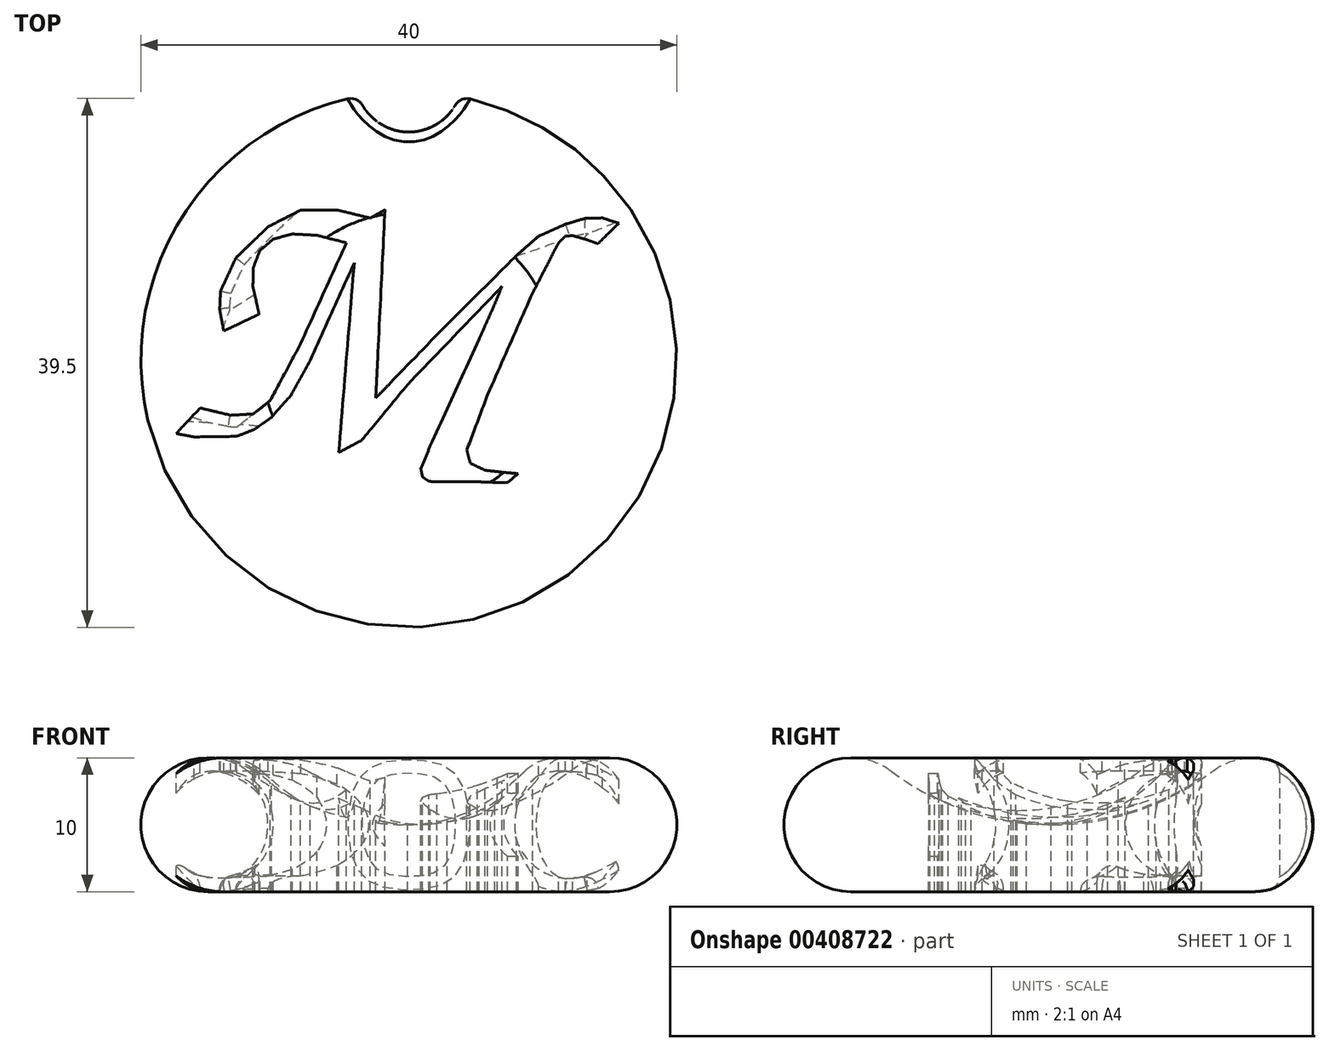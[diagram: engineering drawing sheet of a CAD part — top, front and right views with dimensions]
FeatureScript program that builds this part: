
annotation { "Feature Type Name" : "Feature", "Feature Type Description" : "" }
export const myFeature = defineFeature(function(context is Context, id is Id, definition is map)
    precondition{}
    {
        {
            var Q0;
            Q0=qCreatedBy(makeId("Front.planeOp"),FACE);
            var sketch = newSketch(context, id + "F0", { "sketchPlane" : qUnion([Q0])});
            skArc(sketch, "E0", {"start": v(-12, 9) * mm, "mid": v(-19.74, 6.58) * mm, "end": v(-15, 0) * mm});
            skArc(sketch, "E1", {"start": v(-12, 9) * mm, "mid": v(-6.32, 6.03) * mm, "end": v(0, 5) * mm});
            skLineSegment(sketch, "E2", {"start": v(-15, 0) * mm, "end": v(0, 0) * mm});
            skLineSegment(sketch, "E3", {"start": v(0, 0) * mm, "end": v(0, 5) * mm});
            skSolve(sketch);
        }
        {
            var Q0;
            Q0=makeQuery(id+"F0.imprint","IMPRINT",FACE,{"disambiguationData":[TD([[makeQuery(id+"F0.imprint","IMPRINT",EDGE,{"derivedFrom":sQuery(id+"F0.wireOp",EDGE,"E0")}),1.0]])]});
            var Q1;
            Q1=sQuery(id+"F0.wireOp",EDGE,"E3");
            revolve(context, id + "F1", {"entities" : qUnion([Q0]), "axis" : qUnion([Q1]), "revolveType" : RevolveType.FULL});
        }
        {
            var Q0;
            Q0=qCreatedBy(makeId("Top.planeOp"),FACE);
            cPlane(context, id + "F2", {"entities" : qUnion([Q0]), "cplaneType" : CPlaneType.OFFSET, "offset" : 10 * mm, "width" : 150 * mm, "height" : 150 * mm});
        }
        {
            var Q0;
            Q0=qCreatedBy(id+"F2.planeOp",FACE);
            var sketch = newSketch(context, id + "F3", { "sketchPlane" : qUnion([Q0])});
            skLineSegment(sketch, "E4", {"start": v(8.16, -8.52) * mm, "end": v(6.96, -8.41) * mm});
            skLineSegment(sketch, "E5", {"start": v(6.96, -8.41) * mm, "end": v(5.68, -8.26) * mm});
            skLineSegment(sketch, "E6", {"start": v(5.68, -8.26) * mm, "end": v(4.58, -7.74) * mm});
            skLineSegment(sketch, "E7", {"start": v(4.58, -7.74) * mm, "end": v(4.33, -6.76) * mm});
            skLineSegment(sketch, "E8", {"start": v(4.33, -6.76) * mm, "end": v(5.89, -2.6) * mm});
            skLineSegment(sketch, "E9", {"start": v(5.89, -2.6) * mm, "end": v(9.23, 4.96) * mm});
            skLineSegment(sketch, "E10", {"start": v(9.23, 4.96) * mm, "end": v(11.16, 8.7) * mm});
            skLineSegment(sketch, "E11", {"start": v(11.16, 8.7) * mm, "end": v(11.7, 9.22) * mm});
            skLineSegment(sketch, "E12", {"start": v(11.7, 9.22) * mm, "end": v(12.22, 9.26) * mm});
            skLineSegment(sketch, "E13", {"start": v(12.22, 9.26) * mm, "end": v(13.3, 8.95) * mm});
            skLineSegment(sketch, "E14", {"start": v(13.3, 8.95) * mm, "end": v(14.1, 8.65) * mm});
            skLineSegment(sketch, "E15", {"start": v(14.1, 8.65) * mm, "end": v(15.67, 10.18) * mm});
            skLineSegment(sketch, "E16", {"start": v(15.67, 10.18) * mm, "end": v(14.46, 10.58) * mm});
            skLineSegment(sketch, "E17", {"start": v(14.46, 10.58) * mm, "end": v(13.23, 10.57) * mm});
            skLineSegment(sketch, "E18", {"start": v(13.23, 10.57) * mm, "end": v(11.7, 10.11) * mm});
            skLineSegment(sketch, "E19", {"start": v(11.7, 10.11) * mm, "end": v(9.67, 9.2) * mm});
            skLineSegment(sketch, "E20", {"start": v(9.67, 9.2) * mm, "end": v(8.04, 7.78) * mm});
            skLineSegment(sketch, "E21", {"start": v(8.04, 7.78) * mm, "end": v(2.86, 2.64) * mm});
            skLineSegment(sketch, "E22", {"start": v(2.86, 2.64) * mm, "end": v(-1.5, -1.88) * mm});
            skLineSegment(sketch, "E23", {"start": v(-1.5, -1.88) * mm, "end": v(-2.47, -2.87) * mm});
            skLineSegment(sketch, "E24", {"start": v(-2.47, -2.87) * mm, "end": v(-1.78, 11.19) * mm});
            skLineSegment(sketch, "E25", {"start": v(-1.78, 11.19) * mm, "end": v(-2.88, 10.57) * mm});
            skLineSegment(sketch, "E26", {"start": v(-2.88, 10.57) * mm, "end": v(-5.37, 11.18) * mm});
            skLineSegment(sketch, "E27", {"start": v(-5.37, 11.18) * mm, "end": v(-8.07, 11.16) * mm});
            skLineSegment(sketch, "E28", {"start": v(-8.07, 11.16) * mm, "end": v(-10.5, 9.93) * mm});
            skLineSegment(sketch, "E29", {"start": v(-10.5, 9.93) * mm, "end": v(-12.92, 7.6) * mm});
            skLineSegment(sketch, "E30", {"start": v(-12.92, 7.6) * mm, "end": v(-14.06, 5.12) * mm});
            skLineSegment(sketch, "E31", {"start": v(-14.06, 5.12) * mm, "end": v(-14.12, 3.75) * mm});
            skLineSegment(sketch, "E32", {"start": v(-14.12, 3.75) * mm, "end": v(-13.82, 2.13) * mm});
            skLineSegment(sketch, "E33", {"start": v(-13.82, 2.13) * mm, "end": v(-11.18, 3.39) * mm});
            skLineSegment(sketch, "E34", {"start": v(-11.18, 3.39) * mm, "end": v(-11.64, 5.43) * mm});
            skLineSegment(sketch, "E35", {"start": v(-11.64, 5.43) * mm, "end": v(-11.63, 6.85) * mm});
            skLineSegment(sketch, "E36", {"start": v(-11.63, 6.85) * mm, "end": v(-11.12, 8.15) * mm});
            skLineSegment(sketch, "E37", {"start": v(-11.12, 8.15) * mm, "end": v(-10.13, 9) * mm});
            skLineSegment(sketch, "E38", {"start": v(-10.13, 9) * mm, "end": v(-8.7, 9.38) * mm});
            skLineSegment(sketch, "E39", {"start": v(-8.7, 9.38) * mm, "end": v(-6.87, 9.29) * mm});
            skLineSegment(sketch, "E40", {"start": v(-6.87, 9.29) * mm, "end": v(-4.66, 8.72) * mm});
            skLineSegment(sketch, "E41", {"start": v(-4.66, 8.72) * mm, "end": v(-8.1, 1.17) * mm});
            skLineSegment(sketch, "E42", {"start": v(-8.1, 1.17) * mm, "end": v(-10.34, -3.06) * mm});
            skLineSegment(sketch, "E43", {"start": v(-10.34, -3.06) * mm, "end": v(-11.61, -4.06) * mm});
            skLineSegment(sketch, "E44", {"start": v(-11.61, -4.06) * mm, "end": v(-13.3, -4.16) * mm});
            skLineSegment(sketch, "E45", {"start": v(-13.3, -4.16) * mm, "end": v(-15.58, -3.62) * mm});
            skLineSegment(sketch, "E46", {"start": v(-15.58, -3.62) * mm, "end": v(-17.37, -5.52) * mm});
            skLineSegment(sketch, "E47", {"start": v(-17.37, -5.52) * mm, "end": v(-16.04, -5.78) * mm});
            skLineSegment(sketch, "E48", {"start": v(-16.04, -5.78) * mm, "end": v(-12.85, -5.73) * mm});
            skLineSegment(sketch, "E49", {"start": v(-12.85, -5.73) * mm, "end": v(-11.5, -5.2) * mm});
            skLineSegment(sketch, "E50", {"start": v(-11.5, -5.2) * mm, "end": v(-10.26, -4.32) * mm});
            skLineSegment(sketch, "E51", {"start": v(-10.26, -4.32) * mm, "end": v(-8.8, -2.68) * mm});
            skLineSegment(sketch, "E52", {"start": v(-8.8, -2.68) * mm, "end": v(-7.38, -0.06) * mm});
            skLineSegment(sketch, "E53", {"start": v(-7.38, -0.06) * mm, "end": v(-4.08, 7.22) * mm});
            skLineSegment(sketch, "E54", {"start": v(-4.08, 7.22) * mm, "end": v(-5.23, -6.95) * mm});
            skLineSegment(sketch, "E55", {"start": v(-5.23, -6.95) * mm, "end": v(-3.51, -6.02) * mm});
            skLineSegment(sketch, "E56", {"start": v(-3.51, -6.02) * mm, "end": v(-0.11, -1.89) * mm});
            skLineSegment(sketch, "E57", {"start": v(-0.11, -1.89) * mm, "end": v(6.95, 5.47) * mm});
            skLineSegment(sketch, "E58", {"start": v(6.95, 5.47) * mm, "end": v(6.41, 4.15) * mm});
            skLineSegment(sketch, "E59", {"start": v(6.41, 4.15) * mm, "end": v(5.23, 1.5) * mm});
            skLineSegment(sketch, "E60", {"start": v(5.23, 1.5) * mm, "end": v(1.6, -6.43) * mm});
            skLineSegment(sketch, "E61", {"start": v(1.6, -6.43) * mm, "end": v(0.9, -8.17) * mm});
            skLineSegment(sketch, "E62", {"start": v(0.9, -8.17) * mm, "end": v(1.02, -8.77) * mm});
            skLineSegment(sketch, "E63", {"start": v(1.02, -8.77) * mm, "end": v(1.5, -9.1) * mm});
            skLineSegment(sketch, "E64", {"start": v(1.5, -9.1) * mm, "end": v(2.1, -9.14) * mm});
            skLineSegment(sketch, "E65", {"start": v(2.1, -9.14) * mm, "end": v(5.12, -9.13) * mm});
            skLineSegment(sketch, "E66", {"start": v(5.12, -9.13) * mm, "end": v(6.6, -9.19) * mm});
            skLineSegment(sketch, "E67", {"start": v(6.6, -9.19) * mm, "end": v(7.38, -9.19) * mm});
            skLineSegment(sketch, "E68", {"start": v(7.38, -9.19) * mm, "end": v(8.16, -8.52) * mm});
            skSolve(sketch);
        }
        {
            var Q0;
            Q0=makeQuery(id+"F3.imprint","IMPRINT",FACE,{"disambiguationData":[TD([[makeQuery(id+"F3.imprint","IMPRINT",EDGE,{"derivedFrom":sQuery(id+"F3.wireOp",EDGE,"E4")}),1.0]])]});
            extrude(context, id + "F4", {"entities" : qUnion([Q0]), "operationType" : NewBodyOperationType.REMOVE, "oppositeDirection" : true, "depth" : 25 * mm});
        }
        {
            var Q0;
            Q0=qCreatedBy(makeId("Front.planeOp"),FACE);
            var sketch = newSketch(context, id + "F5", { "sketchPlane" : qUnion([Q0])});
            skCircle(sketch, "E69", {"center": v(-15, 5) * mm, "radius": 4 * mm});
            skSolve(sketch);
        }
        {
            var Q0;
            Q0=qSketchRegion(id+"F5",true);
            var Q1;
            Q1=sQuery(id+"F0.wireOp",EDGE,"E3");
            revolve(context, id + "F6", {"operationType" : NewBodyOperationType.ADD, "entities" : qUnion([Q0]), "axis" : qUnion([Q1]), "revolveType" : RevolveType.FULL});
        }
        {
            var Q0;
            Q0=qCreatedBy(makeId("Top.planeOp"),FACE);
            var sketch = newSketch(context, id + "F7", { "sketchPlane" : qUnion([Q0])});
            skCircle(sketch, "E70", {"center": v(0, 21) * mm, "radius": 4 * mm});
            skSolve(sketch);
        }
        {
            var Q0;
            Q0=makeQuery(id+"F7.imprint","IMPRINT",FACE,{"disambiguationData":[TD([[makeQuery(id+"F7.imprint","IMPRINT",EDGE,{"derivedFrom":sQuery(id+"F7.wireOp",EDGE,"E70")}),1.0]])]});
            extrude(context, id + "F8", {"entities" : qUnion([Q0]), "operationType" : NewBodyOperationType.REMOVE, "depth" : 25 * mm});
        }
        {
            var Q0;
            Q0=makeQuery(id+"F8.boolean.opBoolean","INTERSECT",EDGE,{"derivedFrom":[makeQuery(id+"F4.boolean.opBoolean","SPLIT",FACE,{"disambiguationData":[TD([makeQuery(id+"F1.opRevolve","SWEPT_FACE",FACE,{"disambiguationData":[OSD([sQuery(id+"F0.wireOp",EDGE,"E2")])]})])],"derivedFrom":makeQuery(id+"F1.opRevolve","SWEPT_FACE",FACE,{"disambiguationData":[OSD([sQuery(id+"F0.wireOp",EDGE,"E0")])]})}),makeQuery(id+"F8.opExtrude","SWEPT_FACE",FACE,{"disambiguationData":[OSD([sQuery(id+"F7.wireOp",EDGE,"E70")])]})]});
            fillet(context, id + "F9", {"entities" : qUnion([Q0]), "radius" : 1 * mm, "tangentPropagation" : true, "allowEdgeOverflow" : false});
        }
        {
            var Q0;
            Q0=makeQuery(id+"F6.boolean.opBoolean","INTERSECT",EDGE,{"disambiguationData":[OD(0.0)],"derivedFrom":[makeQuery(id+"F4.boolean.opBoolean","COPY",FACE,{"derivedFrom":makeQuery(id+"F4.opExtrude","SWEPT_FACE",FACE,{"disambiguationData":[OSD([sQuery(id+"F3.wireOp",EDGE,"E48")])]})}),makeQuery(id+"F6.opRevolve","SWEPT_FACE",FACE,{"disambiguationData":[OSD([sQuery(id+"F5.wireOp",EDGE,"E69")])]})]});
            fillet(context, id + "F10", {"entities" : qUnion([Q0]), "radius" : 1 * mm, "tangentPropagation" : true, "allowEdgeOverflow" : false});
        }
        {
            var Q0;
            Q0=makeQuery(id+"F6.boolean.opBoolean","INTERSECT",EDGE,{"disambiguationData":[OD(0.0)],"derivedFrom":[makeQuery(id+"F4.boolean.opBoolean","COPY",FACE,{"derivedFrom":makeQuery(id+"F4.opExtrude","SWEPT_FACE",FACE,{"disambiguationData":[OSD([sQuery(id+"F3.wireOp",EDGE,"E45")])]})}),makeQuery(id+"F6.opRevolve","SWEPT_FACE",FACE,{"disambiguationData":[OSD([sQuery(id+"F5.wireOp",EDGE,"E69")])]})]});
            fillet(context, id + "F11", {"entities" : qUnion([Q0]), "radius" : 1 * mm, "tangentPropagation" : true, "allowEdgeOverflow" : false});
        }
        {
            var Q0;
            Q0=makeQuery(id+"F6.boolean.opBoolean","INTERSECT",EDGE,{"disambiguationData":[OD(1.0)],"derivedFrom":[makeQuery(id+"F4.boolean.opBoolean","COPY",FACE,{"derivedFrom":makeQuery(id+"F4.opExtrude","SWEPT_FACE",FACE,{"disambiguationData":[OSD([sQuery(id+"F3.wireOp",EDGE,"E44")])]})}),makeQuery(id+"F6.opRevolve","SWEPT_FACE",FACE,{"disambiguationData":[OSD([sQuery(id+"F5.wireOp",EDGE,"E69")])]})]});
            fillet(context, id + "F12", {"entities" : qUnion([Q0]), "radius" : 1 * mm, "tangentPropagation" : true, "allowEdgeOverflow" : false});
        }
        {
            var Q0;
            Q0=makeQuery(id+"F6.boolean.opBoolean","INTERSECT",EDGE,{"disambiguationData":[OD(1.0)],"derivedFrom":[makeQuery(id+"F4.boolean.opBoolean","COPY",FACE,{"derivedFrom":makeQuery(id+"F4.opExtrude","SWEPT_FACE",FACE,{"disambiguationData":[OSD([sQuery(id+"F3.wireOp",EDGE,"E32")])]})}),makeQuery(id+"F6.opRevolve","SWEPT_FACE",FACE,{"disambiguationData":[OSD([sQuery(id+"F5.wireOp",EDGE,"E69")])]})]});
            var Q1;
            Q1=makeQuery(id+"F6.boolean.opBoolean","INTERSECT",EDGE,{"disambiguationData":[OD(1.0)],"derivedFrom":[makeQuery(id+"F4.boolean.opBoolean","COPY",FACE,{"derivedFrom":makeQuery(id+"F4.opExtrude","SWEPT_FACE",FACE,{"disambiguationData":[OSD([sQuery(id+"F3.wireOp",EDGE,"E31")])]})}),makeQuery(id+"F6.opRevolve","SWEPT_FACE",FACE,{"disambiguationData":[OSD([sQuery(id+"F5.wireOp",EDGE,"E69")])]})]});
            var Q2;
            Q2=makeQuery(id+"F6.boolean.opBoolean","INTERSECT",EDGE,{"disambiguationData":[OD(1.0)],"derivedFrom":[makeQuery(id+"F4.boolean.opBoolean","COPY",FACE,{"derivedFrom":makeQuery(id+"F4.opExtrude","SWEPT_FACE",FACE,{"disambiguationData":[OSD([sQuery(id+"F3.wireOp",EDGE,"E30")])]})}),makeQuery(id+"F6.opRevolve","SWEPT_FACE",FACE,{"disambiguationData":[OSD([sQuery(id+"F5.wireOp",EDGE,"E69")])]})]});
            var Q3;
            Q3=makeQuery(id+"F6.boolean.opBoolean","INTERSECT",EDGE,{"disambiguationData":[OD(1.0)],"derivedFrom":[makeQuery(id+"F4.boolean.opBoolean","COPY",FACE,{"derivedFrom":makeQuery(id+"F4.opExtrude","SWEPT_FACE",FACE,{"disambiguationData":[OSD([sQuery(id+"F3.wireOp",EDGE,"E29")])]})}),makeQuery(id+"F6.opRevolve","SWEPT_FACE",FACE,{"disambiguationData":[OSD([sQuery(id+"F5.wireOp",EDGE,"E69")])]})]});
            var Q4;
            Q4=makeQuery(id+"F6.boolean.opBoolean","INTERSECT",EDGE,{"disambiguationData":[OD(1.0)],"derivedFrom":[makeQuery(id+"F4.boolean.opBoolean","COPY",FACE,{"derivedFrom":makeQuery(id+"F4.opExtrude","SWEPT_FACE",FACE,{"disambiguationData":[OSD([sQuery(id+"F3.wireOp",EDGE,"E33")])]})}),makeQuery(id+"F6.opRevolve","SWEPT_FACE",FACE,{"disambiguationData":[OSD([sQuery(id+"F5.wireOp",EDGE,"E69")])]})]});
            fillet(context, id + "F13", {"entities" : qUnion([Q0, Q1, Q2, Q3, Q4]), "radius" : 1 * mm, "tangentPropagation" : true, "allowEdgeOverflow" : false});
        }
        {
            var Q0;
            Q0=makeQuery(id+"F6.boolean.opBoolean","INTERSECT",EDGE,{"disambiguationData":[OD(0.0)],"derivedFrom":[makeQuery(id+"F4.boolean.opBoolean","COPY",FACE,{"derivedFrom":makeQuery(id+"F4.opExtrude","SWEPT_FACE",FACE,{"disambiguationData":[OSD([sQuery(id+"F3.wireOp",EDGE,"E15")])]})}),makeQuery(id+"F6.opRevolve","SWEPT_FACE",FACE,{"disambiguationData":[OSD([sQuery(id+"F5.wireOp",EDGE,"E69")])]})]});
            fillet(context, id + "F14", {"entities" : qUnion([Q0]), "radius" : 1 * mm, "tangentPropagation" : true, "allowEdgeOverflow" : false});
        }
        {
            var Q0;
            Q0=makeQuery(id+"F6.boolean.opBoolean","INTERSECT",EDGE,{"disambiguationData":[OD(0.0)],"derivedFrom":[makeQuery(id+"F4.boolean.opBoolean","COPY",FACE,{"derivedFrom":makeQuery(id+"F4.opExtrude","SWEPT_FACE",FACE,{"disambiguationData":[OSD([sQuery(id+"F3.wireOp",EDGE,"E19")])]})}),makeQuery(id+"F6.opRevolve","SWEPT_FACE",FACE,{"disambiguationData":[OSD([sQuery(id+"F5.wireOp",EDGE,"E69")])]})]});
            var Q1;
            Q1=makeQuery(id+"F6.boolean.opBoolean","INTERSECT",EDGE,{"disambiguationData":[OD(0.0)],"derivedFrom":[makeQuery(id+"F4.boolean.opBoolean","COPY",FACE,{"derivedFrom":makeQuery(id+"F4.opExtrude","SWEPT_FACE",FACE,{"disambiguationData":[OSD([sQuery(id+"F3.wireOp",EDGE,"E18")])]})}),makeQuery(id+"F6.opRevolve","SWEPT_FACE",FACE,{"disambiguationData":[OSD([sQuery(id+"F5.wireOp",EDGE,"E69")])]})]});
            var Q2;
            Q2=makeQuery(id+"F6.boolean.opBoolean","INTERSECT",EDGE,{"disambiguationData":[OD(0.0)],"derivedFrom":[makeQuery(id+"F4.boolean.opBoolean","COPY",FACE,{"derivedFrom":makeQuery(id+"F4.opExtrude","SWEPT_FACE",FACE,{"disambiguationData":[OSD([sQuery(id+"F3.wireOp",EDGE,"E17")])]})}),makeQuery(id+"F6.opRevolve","SWEPT_FACE",FACE,{"disambiguationData":[OSD([sQuery(id+"F5.wireOp",EDGE,"E69")])]})]});
            fillet(context, id + "F15", {"entities" : qUnion([Q0, Q1, Q2]), "radius" : 1 * mm, "tangentPropagation" : true, "allowEdgeOverflow" : false});
        }
    });
